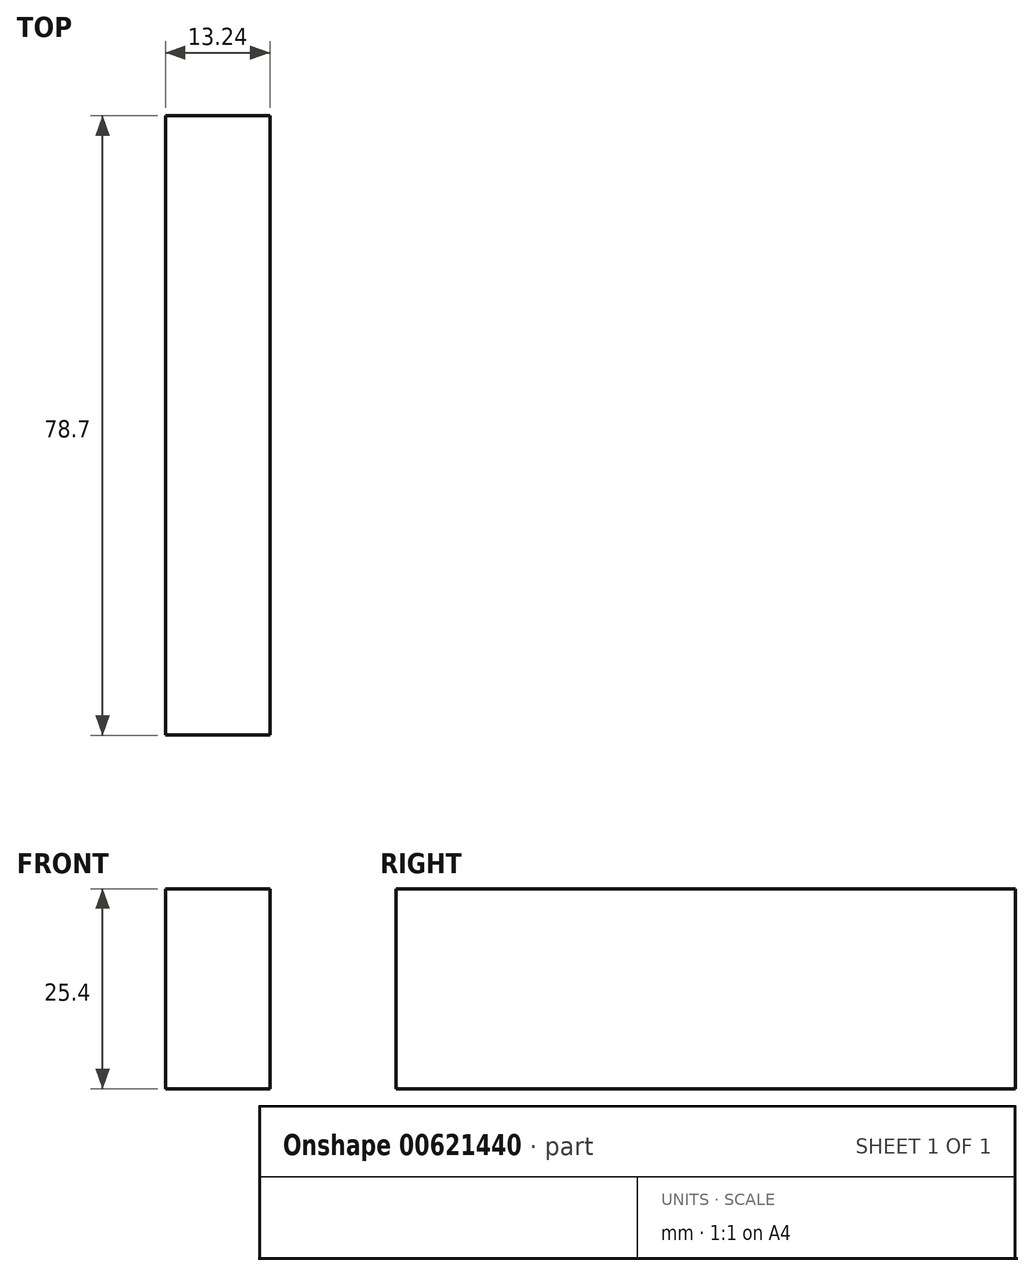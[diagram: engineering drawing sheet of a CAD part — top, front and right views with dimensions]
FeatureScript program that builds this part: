
annotation { "Feature Type Name" : "Feature", "Feature Type Description" : "" }
export const myFeature = defineFeature(function(context is Context, id is Id, definition is map)
    precondition{}
    {
        {
            var Q0;
            Q0=qCreatedBy(makeId("Top.planeOp"),FACE);
            var sketch = newSketch(context, id + "F0", { "sketchPlane" : qUnion([Q0])});
            skLineSegment(sketch, "E0.bottom", {"start": v(-6.62, 62.6) * mm, "end": v(6.62, 62.6) * mm});
            skLineSegment(sketch, "E0.top", {"start": v(-6.62, -16.1) * mm, "end": v(6.62, -16.1) * mm});
            skLineSegment(sketch, "E0.left", {"start": v(-6.62, 62.6) * mm, "end": v(-6.62, 57.23) * mm});
            skLineSegment(sketch, "E0.right", {"start": v(6.62, 62.6) * mm, "end": v(6.62, 57.23) * mm});
            skLineSegment(sketch, "E1.trimOffspring", {"start": v(6.62, 45.07) * mm, "end": v(6.62, -16.1) * mm});
            skLineSegment(sketch, "E2.trimOffspring", {"start": v(-6.62, 45.07) * mm, "end": v(-6.62, -16.1) * mm});
            skLineSegment(sketch, "E3", {"start": v(-6.62, 57.23) * mm, "end": v(-6.62, 45.07) * mm});
            skLineSegment(sketch, "E4", {"start": v(6.62, 57.23) * mm, "end": v(6.62, 45.07) * mm});
            skSolve(sketch);
        }
        {
            var Q0;
            Q0=makeQuery(id+"F0.imprint","IMPRINT",FACE,{"disambiguationData":[TD([[makeQuery(id+"F0.imprint","IMPRINT",EDGE,{"derivedFrom":sQuery(id+"F0.wireOp",EDGE,"E0.bottom")}),-1.0]])]});
            extrude(context, id + "F1", {"entities" : qUnion([Q0]), "depth" : 25.4 * mm, "offsetDistance" : 25.4 * mm, "symmetric" : true});
        }
    });
